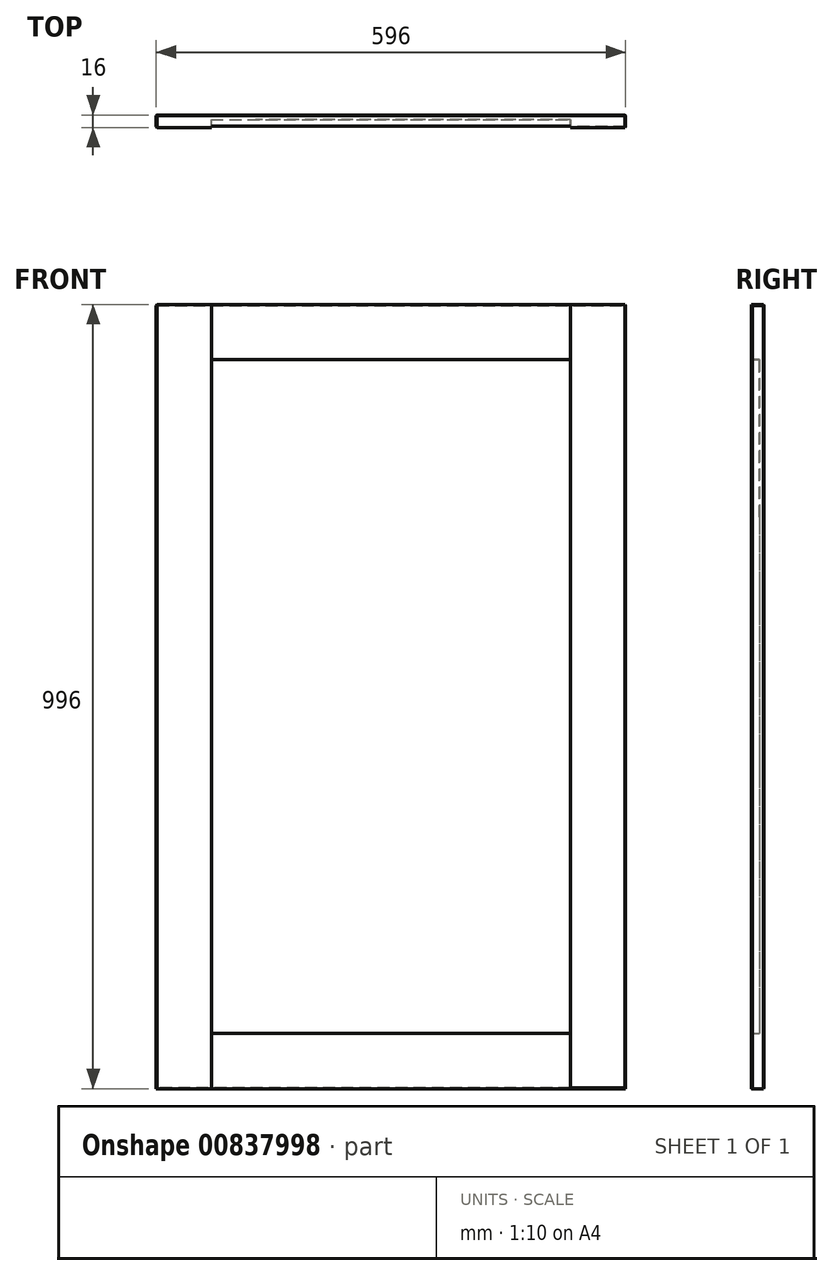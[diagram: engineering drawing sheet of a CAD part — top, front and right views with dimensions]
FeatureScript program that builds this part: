
annotation { "Feature Type Name" : "Feature", "Feature Type Description" : "" }
export const myFeature = defineFeature(function(context is Context, id is Id, definition is map)
    precondition{}
    {
        {
            var Q0;
            Q0=qCreatedBy(makeId("Front.planeOp"),FACE);
            var sketch = newSketch(context, id + "F0", { "sketchPlane" : qUnion([Q0])});
            skLineSegment(sketch, "E0.bottom", {"start": v(0, 0) * mm, "end": v(35.9, 0) * mm});
            skLineSegment(sketch, "E0.top", {"start": v(0, 30.12) * mm, "end": v(35.9, 30.12) * mm});
            skLineSegment(sketch, "E0.left", {"start": v(0, 0) * mm, "end": v(0, 30.12) * mm});
            skLineSegment(sketch, "E0.right", {"start": v(35.9, 0) * mm, "end": v(35.9, 30.12) * mm});
            skSolve(sketch);
        }
        {
            var Q0;
            Q0=makeQuery(id+"F0.imprint","IMPRINT",FACE,{"disambiguationData":[TD([[makeQuery(id+"F0.imprint","IMPRINT",EDGE,{"derivedFrom":sQuery(id+"F0.wireOp",EDGE,"E0.bottom")}),1.0]])]});
            extrude(context, id + "F1", {"entities" : qUnion([Q0]), "depth" : 16 * mm, "offsetDistance" : 25.4 * mm});
        }
        {
            var Q0;
            Q0=makeQuery(id+"F1.opExtrude","SWEPT_FACE",FACE,{"disambiguationData":[OSD([sQuery(id+"F0.wireOp",EDGE,"E0.left")])]});
            extrude(context, id + "F2", {"entities" : qUnion([Q0]), "operationType" : NewBodyOperationType.ADD, "oppositeDirection" : true, "depth" : 196 * mm, "offsetDistance" : 25 * mm});
        }
        {
            var Q0;
            {var subQ0=sQuery(id+"F0.wireOp",EDGE,"E0.bottom");Q0=makeQuery(id+"F2.boolean.opBoolean","MERGE",FACE,{"derivedFrom":[makeQuery(id+"F1.opExtrude","SWEPT_FACE",FACE,{"disambiguationData":[OSD([subQ0])]}),makeQuery(id+"F2.opExtrude","SWEPT_FACE",FACE,{"disambiguationData":[OSD([subQ0,sQuery(id+"F0.wireOp",EDGE,"E0.left")])]})]});}
            extrude(context, id + "F3", {"entities" : qUnion([Q0]), "operationType" : NewBodyOperationType.ADD, "oppositeDirection" : true, "depth" : 796 * mm, "offsetDistance" : 25 * mm});
        }
        {
            var Q0;
            {var subQ0=sQuery(id+"F0.wireOp",EDGE,"E0.left");var subQ1=sQuery(id+"F0.wireOp",EDGE,"E0.bottom");Q0=makeQuery(id+"F3.boolean.opBoolean","MERGE",FACE,{"derivedFrom":[makeQuery(id+"F2.boolean.opBoolean","MERGE",FACE,{"derivedFrom":[makeQuery(id+"F1.opExtrude","CAP_FACE",FACE,{"disambiguationData":[OSD([subQ1,sQuery(id+"F0.wireOp",EDGE,"E0.top"),subQ0,sQuery(id+"F0.wireOp",EDGE,"E0.right")])],"isStart":false}),makeQuery(id+"F2.opExtrude","SWEPT_FACE",FACE,{"disambiguationData":[OSD([subQ0]),TDD([makeQuery(id+"F1.opExtrude","CAP_EDGE",EDGE,{"disambiguationData":[OSD([subQ0])],"isStart":false})])]})]}),makeQuery(id+"F3.opExtrude","SWEPT_FACE",FACE,{"disambiguationData":[OSD([subQ1,subQ0]),TDD([makeQuery(id+"F2.boolean.opBoolean","MERGE",EDGE,{"derivedFrom":[makeQuery(id+"F1.opExtrude","CAP_EDGE",EDGE,{"disambiguationData":[OSD([subQ1])],"isStart":false}),makeQuery(id+"F2.opExtrude","SWEPT_EDGE",EDGE,{"disambiguationData":[OSD([subQ1,subQ0]),TDD([makeQuery(id+"F1.opExtrude","CAP_VERTEX",VERTEX,{"disambiguationData":[OSD([subQ1,subQ0])],"isStart":false})])]})]})])]})]});}
            var sketch = newSketch(context, id + "F4", { "sketchPlane" : qUnion([Q0])});
            skLineSegment(sketch, "E1.bottom", {"start": v(0, 796) * mm, "end": v(42.19, 796) * mm});
            skLineSegment(sketch, "E1.top", {"start": v(0, 751.57) * mm, "end": v(42.19, 751.57) * mm});
            skLineSegment(sketch, "E1.left", {"start": v(0, 796) * mm, "end": v(0, 751.57) * mm});
            skLineSegment(sketch, "E1.right", {"start": v(42.19, 796) * mm, "end": v(42.19, 751.57) * mm});
            skLineSegment(sketch, "E2.bottom", {"start": v(196, 796) * mm, "end": v(153.6, 796) * mm});
            skLineSegment(sketch, "E2.top", {"start": v(196, 746.75) * mm, "end": v(153.6, 746.75) * mm});
            skLineSegment(sketch, "E2.left", {"start": v(196, 796) * mm, "end": v(196, 746.75) * mm});
            skLineSegment(sketch, "E2.right", {"start": v(153.6, 796) * mm, "end": v(153.6, 746.75) * mm});
            skSolve(sketch);
        }
        {
            var Q0;
            Q0=makeQuery(id+"F4.imprint","IMPRINT",FACE,{"disambiguationData":[TD([[makeQuery(id+"F4.imprint","IMPRINT",EDGE,{"derivedFrom":sQuery(id+"F4.wireOp",EDGE,"E1.bottom")}),-1.0]])]});
            var Q1;
            Q1=makeQuery(id+"F4.imprint","IMPRINT",FACE,{"disambiguationData":[TD([[makeQuery(id+"F4.imprint","IMPRINT",EDGE,{"derivedFrom":sQuery(id+"F4.wireOp",EDGE,"E2.bottom")}),-1.0]])]});
            extrude(context, id + "F5", {"entities" : qUnion([Q0, Q1]), "operationType" : NewBodyOperationType.ADD, "depth" : 25 * mm, "offsetDistance" : 25 * mm});
        }
        {
            var Q0;
            {var subQ0=sQuery(id+"F0.wireOp",EDGE,"E0.left");var subQ1=sQuery(id+"F0.wireOp",EDGE,"E0.bottom");Q0=makeQuery(id+"F3.boolean.opBoolean","MERGE",FACE,{"derivedFrom":[makeQuery(id+"F2.boolean.opBoolean","MERGE",FACE,{"derivedFrom":[makeQuery(id+"F1.opExtrude","CAP_FACE",FACE,{"disambiguationData":[OSD([subQ1,sQuery(id+"F0.wireOp",EDGE,"E0.top"),subQ0,sQuery(id+"F0.wireOp",EDGE,"E0.right")])],"isStart":false}),makeQuery(id+"F2.opExtrude","SWEPT_FACE",FACE,{"disambiguationData":[OSD([subQ0]),TDD([makeQuery(id+"F1.opExtrude","CAP_EDGE",EDGE,{"disambiguationData":[OSD([subQ0])],"isStart":false})])]})]}),makeQuery(id+"F3.opExtrude","SWEPT_FACE",FACE,{"disambiguationData":[OSD([subQ1,subQ0]),TDD([makeQuery(id+"F2.boolean.opBoolean","MERGE",EDGE,{"derivedFrom":[makeQuery(id+"F1.opExtrude","CAP_EDGE",EDGE,{"disambiguationData":[OSD([subQ1])],"isStart":false}),makeQuery(id+"F2.opExtrude","SWEPT_EDGE",EDGE,{"disambiguationData":[OSD([subQ1,subQ0]),TDD([makeQuery(id+"F1.opExtrude","CAP_VERTEX",VERTEX,{"disambiguationData":[OSD([subQ1,subQ0])],"isStart":false})])]})]})])]})]});}
            var sketch = newSketch(context, id + "F6", { "sketchPlane" : qUnion([Q0])});
            skLineSegment(sketch, "E3.bottom", {"start": v(196, 0) * mm, "end": v(163.38, 0) * mm});
            skLineSegment(sketch, "E3.top", {"start": v(196, 46.55) * mm, "end": v(163.38, 46.55) * mm});
            skLineSegment(sketch, "E3.left", {"start": v(196, 0) * mm, "end": v(196, 46.55) * mm});
            skLineSegment(sketch, "E3.right", {"start": v(163.38, 0) * mm, "end": v(163.38, 46.55) * mm});
            skLineSegment(sketch, "E4.bottom", {"start": v(0, 0) * mm, "end": v(50.28, 0) * mm});
            skLineSegment(sketch, "E4.top", {"start": v(0, 44.4) * mm, "end": v(50.28, 44.4) * mm});
            skLineSegment(sketch, "E4.left", {"start": v(0, 0) * mm, "end": v(0, 44.4) * mm});
            skLineSegment(sketch, "E4.right", {"start": v(50.28, 0) * mm, "end": v(50.28, 44.4) * mm});
            skSolve(sketch);
        }
        {
            var Q0;
            Q0=makeQuery(id+"F6.imprint","IMPRINT",FACE,{"disambiguationData":[TD([[makeQuery(id+"F6.imprint","IMPRINT",EDGE,{"derivedFrom":sQuery(id+"F6.wireOp",EDGE,"E3.bottom")}),1.0]])]});
            var Q1;
            Q1=makeQuery(id+"F6.imprint","IMPRINT",FACE,{"disambiguationData":[TD([[makeQuery(id+"F6.imprint","IMPRINT",EDGE,{"derivedFrom":sQuery(id+"F6.wireOp",EDGE,"E4.bottom")}),1.0]])]});
            extrude(context, id + "F7", {"entities" : qUnion([Q0, Q1]), "operationType" : NewBodyOperationType.ADD, "depth" : 25 * mm, "offsetDistance" : 25 * mm});
        }
        {
            var Q0;
            Q0=makeQuery(id+"F7.opExtrude","SWEPT_FACE",FACE,{"disambiguationData":[OSD([sQuery(id+"F6.wireOp",EDGE,"E4.right")])]});
            extrude(context, id + "F8", {"entities" : qUnion([Q0]), "operationType" : NewBodyOperationType.ADD, "depth" : 19.72 * mm, "offsetDistance" : 25 * mm});
        }
        {
            var Q0;
            {var subQ0=sQuery(id+"F6.wireOp",EDGE,"E4.top");Q0=makeQuery(id+"F8.boolean.opBoolean","MERGE",FACE,{"derivedFrom":[makeQuery(id+"F7.opExtrude","SWEPT_FACE",FACE,{"disambiguationData":[OSD([subQ0])]}),makeQuery(id+"F8.opExtrude","SWEPT_FACE",FACE,{"disambiguationData":[OSD([subQ0,sQuery(id+"F6.wireOp",EDGE,"E4.right")])]})]});}
            extrude(context, id + "F9", {"entities" : qUnion([Q0]), "operationType" : NewBodyOperationType.ADD, "depth" : 25.6 * mm, "offsetDistance" : 25 * mm});
        }
        {
            var Q0;
            Q0=makeQuery(id+"F7.opExtrude","SWEPT_FACE",FACE,{"disambiguationData":[OSD([sQuery(id+"F6.wireOp",EDGE,"E3.right")])]});
            extrude(context, id + "F10", {"entities" : qUnion([Q0]), "operationType" : NewBodyOperationType.ADD, "depth" : 37.38 * mm, "offsetDistance" : 25 * mm});
        }
        {
            var Q0;
            {var subQ0=sQuery(id+"F6.wireOp",EDGE,"E3.top");Q0=makeQuery(id+"F10.boolean.opBoolean","MERGE",FACE,{"derivedFrom":[makeQuery(id+"F7.opExtrude","SWEPT_FACE",FACE,{"disambiguationData":[OSD([subQ0])]}),makeQuery(id+"F10.opExtrude","SWEPT_FACE",FACE,{"disambiguationData":[OSD([subQ0,sQuery(id+"F6.wireOp",EDGE,"E3.right")])]})]});}
            extrude(context, id + "F11", {"entities" : qUnion([Q0]), "operationType" : NewBodyOperationType.ADD, "depth" : 23.45 * mm, "offsetDistance" : 25 * mm});
        }
        {
            var Q0;
            Q0=makeQuery(id+"F5.opExtrude","SWEPT_FACE",FACE,{"disambiguationData":[OSD([sQuery(id+"F4.wireOp",EDGE,"E1.right")])]});
            extrude(context, id + "F12", {"entities" : qUnion([Q0]), "operationType" : NewBodyOperationType.ADD, "depth" : 27.8 * mm, "offsetDistance" : 25 * mm});
        }
        {
            var Q0;
            {var subQ0=sQuery(id+"F4.wireOp",EDGE,"E1.top");Q0=makeQuery(id+"F12.boolean.opBoolean","MERGE",FACE,{"derivedFrom":[makeQuery(id+"F5.opExtrude","SWEPT_FACE",FACE,{"disambiguationData":[OSD([subQ0])]}),makeQuery(id+"F12.opExtrude","SWEPT_FACE",FACE,{"disambiguationData":[OSD([subQ0,sQuery(id+"F4.wireOp",EDGE,"E1.right")])]})]});}
            extrude(context, id + "F13", {"entities" : qUnion([Q0]), "operationType" : NewBodyOperationType.ADD, "depth" : 25.57 * mm, "offsetDistance" : 25 * mm});
        }
        {
            var Q0;
            Q0=makeQuery(id+"F5.opExtrude","SWEPT_FACE",FACE,{"disambiguationData":[OSD([sQuery(id+"F4.wireOp",EDGE,"E2.top")])]});
            extrude(context, id + "F14", {"entities" : qUnion([Q0]), "operationType" : NewBodyOperationType.ADD, "depth" : 20.75 * mm, "offsetDistance" : 25 * mm});
        }
        {
            var Q0;
            {var subQ0=sQuery(id+"F4.wireOp",EDGE,"E2.right");Q0=makeQuery(id+"F14.boolean.opBoolean","MERGE",FACE,{"derivedFrom":[makeQuery(id+"F5.opExtrude","SWEPT_FACE",FACE,{"disambiguationData":[OSD([subQ0])]}),makeQuery(id+"F14.opExtrude","SWEPT_FACE",FACE,{"disambiguationData":[OSD([sQuery(id+"F4.wireOp",EDGE,"E2.top"),subQ0])]})]});}
            extrude(context, id + "F15", {"entities" : qUnion([Q0]), "operationType" : NewBodyOperationType.ADD, "depth" : 27.6 * mm, "offsetDistance" : 25 * mm});
        }
        {
            var Q0;
            {var subQ0=sQuery(id+"F0.wireOp",EDGE,"E0.left");var subQ1=sQuery(id+"F0.wireOp",EDGE,"E0.bottom");Q0=makeQuery(id+"F3.boolean.opBoolean","MERGE",FACE,{"derivedFrom":[makeQuery(id+"F2.boolean.opBoolean","MERGE",FACE,{"derivedFrom":[makeQuery(id+"F1.opExtrude","CAP_FACE",FACE,{"disambiguationData":[OSD([subQ1,sQuery(id+"F0.wireOp",EDGE,"E0.top"),subQ0,sQuery(id+"F0.wireOp",EDGE,"E0.right")])],"isStart":false}),makeQuery(id+"F2.opExtrude","SWEPT_FACE",FACE,{"disambiguationData":[OSD([subQ0]),TDD([makeQuery(id+"F1.opExtrude","CAP_EDGE",EDGE,{"disambiguationData":[OSD([subQ0])],"isStart":false})])]})]}),makeQuery(id+"F3.opExtrude","SWEPT_FACE",FACE,{"disambiguationData":[OSD([subQ1,subQ0]),TDD([makeQuery(id+"F2.boolean.opBoolean","MERGE",EDGE,{"derivedFrom":[makeQuery(id+"F1.opExtrude","CAP_EDGE",EDGE,{"disambiguationData":[OSD([subQ1])],"isStart":false}),makeQuery(id+"F2.opExtrude","SWEPT_EDGE",EDGE,{"disambiguationData":[OSD([subQ1,subQ0]),TDD([makeQuery(id+"F1.opExtrude","CAP_VERTEX",VERTEX,{"disambiguationData":[OSD([subQ1,subQ0])],"isStart":false})])]})]})])]})]});}
            var sketch = newSketch(context, id + "F16", { "sketchPlane" : qUnion([Q0])});
            skLineSegment(sketch, "E5.bottom", {"start": v(70, 726) * mm, "end": v(126, 726) * mm});
            skLineSegment(sketch, "E5.top", {"start": v(70, 70) * mm, "end": v(126, 70) * mm});
            skLineSegment(sketch, "E5.left", {"start": v(70, 726) * mm, "end": v(70, 70) * mm});
            skLineSegment(sketch, "E5.right", {"start": v(126, 726) * mm, "end": v(126, 70) * mm});
            skSolve(sketch);
        }
        {
            var Q0;
            Q0=makeQuery(id+"F16.imprint","IMPRINT",FACE,{"disambiguationData":[TD([[makeQuery(id+"F16.imprint","IMPRINT",EDGE,{"derivedFrom":sQuery(id+"F16.wireOp",EDGE,"E5.top")}),1.0]])]});
            extrude(context, id + "F17", {"entities" : qUnion([Q0]), "operationType" : NewBodyOperationType.REMOVE, "oppositeDirection" : true, "depth" : 10 * mm, "offsetDistance" : 25 * mm});
        }
        {
            var Q0;
            {var subQ2=sQuery(id+"F0.wireOp",EDGE,"E0.left");var subQ3=sQuery(id+"F0.wireOp",EDGE,"E0.bottom");var subQ4=makeQuery(id+"F1.opExtrude","CAP_FACE",FACE,{"disambiguationData":[OSD([subQ3,sQuery(id+"F0.wireOp",EDGE,"E0.top"),subQ2,sQuery(id+"F0.wireOp",EDGE,"E0.right")])],"isStart":false});var subQ7=makeQuery(id+"F3.opExtrude","SWEPT_FACE",FACE,{"disambiguationData":[OSD([subQ3,subQ2]),TDD([makeQuery(id+"F2.boolean.opBoolean","MERGE",EDGE,{"derivedFrom":[makeQuery(id+"F1.opExtrude","CAP_EDGE",EDGE,{"disambiguationData":[OSD([subQ3])],"isStart":false}),makeQuery(id+"F2.opExtrude","SWEPT_EDGE",EDGE,{"disambiguationData":[OSD([subQ3,subQ2]),TDD([makeQuery(id+"F1.opExtrude","CAP_VERTEX",VERTEX,{"disambiguationData":[OSD([subQ3,subQ2])],"isStart":false})])]})]})])]});var subQ8=makeQuery(id+"F2.opExtrude","SWEPT_FACE",FACE,{"disambiguationData":[OSD([subQ2]),TDD([makeQuery(id+"F1.opExtrude","CAP_EDGE",EDGE,{"disambiguationData":[OSD([subQ2])],"isStart":false})])]});Q0=makeQuery(id+"F17.boolean.opBoolean","SPLIT",FACE,{"disambiguationData":[TD([makeQuery(id+"F1.opExtrude","SWEPT_FACE",FACE,{"disambiguationData":[OSD([subQ3])]})])],"derivedFrom":makeQuery(id+"F3.boolean.opBoolean","MERGE",FACE,{"derivedFrom":[makeQuery(id+"F2.boolean.opBoolean","MERGE",FACE,{"derivedFrom":[subQ4,subQ8]}),subQ7]})});}
            var Q1;
            {var subQ2=sQuery(id+"F4.wireOp",EDGE,"E1.bottom");var subQ3=sQuery(id+"F0.wireOp",EDGE,"E0.left");var subQ4=sQuery(id+"F0.wireOp",EDGE,"E0.bottom");var subQ6=makeQuery(id+"F1.opExtrude","CAP_FACE",FACE,{"disambiguationData":[OSD([subQ4,sQuery(id+"F0.wireOp",EDGE,"E0.top"),subQ3,sQuery(id+"F0.wireOp",EDGE,"E0.right")])],"isStart":false});var subQ7=makeQuery(id+"F2.opExtrude","SWEPT_FACE",FACE,{"disambiguationData":[OSD([subQ3]),TDD([makeQuery(id+"F1.opExtrude","CAP_EDGE",EDGE,{"disambiguationData":[OSD([subQ3])],"isStart":false})])]});var subQ8=makeQuery(id+"F3.opExtrude","SWEPT_FACE",FACE,{"disambiguationData":[OSD([subQ4,subQ3]),TDD([makeQuery(id+"F2.boolean.opBoolean","MERGE",EDGE,{"derivedFrom":[makeQuery(id+"F1.opExtrude","CAP_EDGE",EDGE,{"disambiguationData":[OSD([subQ4])],"isStart":false}),makeQuery(id+"F2.opExtrude","SWEPT_EDGE",EDGE,{"disambiguationData":[OSD([subQ4,subQ3]),TDD([makeQuery(id+"F1.opExtrude","CAP_VERTEX",VERTEX,{"disambiguationData":[OSD([subQ4,subQ3])],"isStart":false})])]})]})])]});Q1=makeQuery(id+"F17.boolean.opBoolean","SPLIT",FACE,{"disambiguationData":[TD([makeQuery(id+"F5.opExtrude","SWEPT_FACE",FACE,{"disambiguationData":[OSD([subQ2])]})])],"derivedFrom":makeQuery(id+"F3.boolean.opBoolean","MERGE",FACE,{"derivedFrom":[makeQuery(id+"F2.boolean.opBoolean","MERGE",FACE,{"derivedFrom":[subQ6,subQ7]}),subQ8]})});}
            extrude(context, id + "F18", {"entities" : qUnion([Q0, Q1]), "operationType" : NewBodyOperationType.REMOVE, "oppositeDirection" : true, "depth" : 2 * mm, "offsetDistance" : 25 * mm});
        }
        {
            var Q0;
            {var subQ0=sQuery(id+"F4.wireOp",EDGE,"E1.right");var subQ1=sQuery(id+"F4.wireOp",EDGE,"E1.top");Q0=makeQuery(id+"F13.boolean.opBoolean","MERGE",FACE,{"derivedFrom":[makeQuery(id+"F12.boolean.opBoolean","MERGE",FACE,{"derivedFrom":[makeQuery(id+"F5.opExtrude","CAP_FACE",FACE,{"disambiguationData":[OSD([sQuery(id+"F4.wireOp",EDGE,"E1.bottom"),subQ1,sQuery(id+"F4.wireOp",EDGE,"E1.left"),subQ0])],"isStart":false}),makeQuery(id+"F12.opExtrude","SWEPT_FACE",FACE,{"disambiguationData":[OSD([subQ0]),TDD([makeQuery(id+"F5.opExtrude","CAP_EDGE",EDGE,{"disambiguationData":[OSD([subQ0])],"isStart":false})])]})]}),makeQuery(id+"F13.opExtrude","SWEPT_FACE",FACE,{"disambiguationData":[OSD([subQ1,subQ0]),TDD([makeQuery(id+"F12.boolean.opBoolean","MERGE",EDGE,{"derivedFrom":[makeQuery(id+"F5.opExtrude","CAP_EDGE",EDGE,{"disambiguationData":[OSD([subQ1])],"isStart":false}),makeQuery(id+"F12.opExtrude","SWEPT_EDGE",EDGE,{"disambiguationData":[OSD([subQ1,subQ0]),TDD([makeQuery(id+"F5.opExtrude","CAP_VERTEX",VERTEX,{"disambiguationData":[OSD([subQ1,subQ0])],"isStart":false})])]})]})])]})]});}
            var Q1;
            {var subQ0=sQuery(id+"F4.wireOp",EDGE,"E2.right");var subQ1=sQuery(id+"F4.wireOp",EDGE,"E2.top");Q1=makeQuery(id+"F15.boolean.opBoolean","MERGE",FACE,{"derivedFrom":[makeQuery(id+"F14.boolean.opBoolean","MERGE",FACE,{"derivedFrom":[makeQuery(id+"F5.opExtrude","CAP_FACE",FACE,{"disambiguationData":[OSD([sQuery(id+"F4.wireOp",EDGE,"E2.bottom"),subQ1,sQuery(id+"F4.wireOp",EDGE,"E2.left"),subQ0])],"isStart":false}),makeQuery(id+"F14.opExtrude","SWEPT_FACE",FACE,{"disambiguationData":[OSD([subQ1]),TDD([makeQuery(id+"F5.opExtrude","CAP_EDGE",EDGE,{"disambiguationData":[OSD([subQ1])],"isStart":false})])]})]}),makeQuery(id+"F15.opExtrude","SWEPT_FACE",FACE,{"disambiguationData":[OSD([subQ1,subQ0]),TDD([makeQuery(id+"F14.boolean.opBoolean","MERGE",EDGE,{"derivedFrom":[makeQuery(id+"F5.opExtrude","CAP_EDGE",EDGE,{"disambiguationData":[OSD([subQ0])],"isStart":false}),makeQuery(id+"F14.opExtrude","SWEPT_EDGE",EDGE,{"disambiguationData":[OSD([subQ1,subQ0]),TDD([makeQuery(id+"F5.opExtrude","CAP_VERTEX",VERTEX,{"disambiguationData":[OSD([subQ1,subQ0])],"isStart":false})])]})]})])]})]});}
            var Q2;
            {var subQ0=sQuery(id+"F6.wireOp",EDGE,"E4.right");var subQ1=sQuery(id+"F6.wireOp",EDGE,"E4.top");Q2=makeQuery(id+"F9.boolean.opBoolean","MERGE",FACE,{"derivedFrom":[makeQuery(id+"F8.boolean.opBoolean","MERGE",FACE,{"derivedFrom":[makeQuery(id+"F7.opExtrude","CAP_FACE",FACE,{"disambiguationData":[OSD([sQuery(id+"F6.wireOp",EDGE,"E4.bottom"),subQ1,sQuery(id+"F6.wireOp",EDGE,"E4.left"),subQ0])],"isStart":false}),makeQuery(id+"F8.opExtrude","SWEPT_FACE",FACE,{"disambiguationData":[OSD([subQ0]),TDD([makeQuery(id+"F7.opExtrude","CAP_EDGE",EDGE,{"disambiguationData":[OSD([subQ0])],"isStart":false})])]})]}),makeQuery(id+"F9.opExtrude","SWEPT_FACE",FACE,{"disambiguationData":[OSD([subQ1,subQ0]),TDD([makeQuery(id+"F8.boolean.opBoolean","MERGE",EDGE,{"derivedFrom":[makeQuery(id+"F7.opExtrude","CAP_EDGE",EDGE,{"disambiguationData":[OSD([subQ1])],"isStart":false}),makeQuery(id+"F8.opExtrude","SWEPT_EDGE",EDGE,{"disambiguationData":[OSD([subQ1,subQ0]),TDD([makeQuery(id+"F7.opExtrude","CAP_VERTEX",VERTEX,{"disambiguationData":[OSD([subQ1,subQ0])],"isStart":false})])]})]})])]})]});}
            var Q3;
            {var subQ0=sQuery(id+"F6.wireOp",EDGE,"E3.right");var subQ1=sQuery(id+"F6.wireOp",EDGE,"E3.top");Q3=makeQuery(id+"F11.boolean.opBoolean","MERGE",FACE,{"derivedFrom":[makeQuery(id+"F10.boolean.opBoolean","MERGE",FACE,{"derivedFrom":[makeQuery(id+"F7.opExtrude","CAP_FACE",FACE,{"disambiguationData":[OSD([sQuery(id+"F6.wireOp",EDGE,"E3.bottom"),subQ1,sQuery(id+"F6.wireOp",EDGE,"E3.left"),subQ0])],"isStart":false}),makeQuery(id+"F10.opExtrude","SWEPT_FACE",FACE,{"disambiguationData":[OSD([subQ0]),TDD([makeQuery(id+"F7.opExtrude","CAP_EDGE",EDGE,{"disambiguationData":[OSD([subQ0])],"isStart":false})])]})]}),makeQuery(id+"F11.opExtrude","SWEPT_FACE",FACE,{"disambiguationData":[OSD([subQ1,subQ0]),TDD([makeQuery(id+"F10.boolean.opBoolean","MERGE",EDGE,{"derivedFrom":[makeQuery(id+"F7.opExtrude","CAP_EDGE",EDGE,{"disambiguationData":[OSD([subQ1])],"isStart":false}),makeQuery(id+"F10.opExtrude","SWEPT_EDGE",EDGE,{"disambiguationData":[OSD([subQ1,subQ0]),TDD([makeQuery(id+"F7.opExtrude","CAP_VERTEX",VERTEX,{"disambiguationData":[OSD([subQ1,subQ0])],"isStart":false})])]})]})])]})]});}
            extrude(context, id + "F19", {"entities" : qUnion([Q0, Q1, Q2, Q3]), "operationType" : NewBodyOperationType.REMOVE, "oppositeDirection" : true, "depth" : 25 * mm, "offsetDistance" : 25 * mm});
        }
        {
            var Q0;
            {var subQ0=sQuery(id+"F4.wireOp",EDGE,"E2.left");var subQ1=sQuery(id+"F0.wireOp",EDGE,"E0.left");var subQ2=sQuery(id+"F0.wireOp",EDGE,"E0.bottom");var subQ3=sQuery(id+"F6.wireOp",EDGE,"E3.left");Q0=makeQuery(id+"F14.boolean.opBoolean","MERGE",FACE,{"derivedFrom":[makeQuery(id+"F11.boolean.opBoolean","MERGE",FACE,{"derivedFrom":[makeQuery(id+"F7.boolean.opBoolean","MERGE",FACE,{"derivedFrom":[makeQuery(id+"F5.boolean.opBoolean","MERGE",FACE,{"derivedFrom":[makeQuery(id+"F3.boolean.opBoolean","MERGE",FACE,{"derivedFrom":[makeQuery(id+"F2.opExtrude","CAP_FACE",FACE,{"disambiguationData":[OSD([subQ1])],"isStart":false}),makeQuery(id+"F3.opExtrude","SWEPT_FACE",FACE,{"disambiguationData":[OSD([subQ2,subQ1]),TDD([makeQuery(id+"F2.opExtrude","CAP_EDGE",EDGE,{"disambiguationData":[OSD([subQ2,subQ1])],"isStart":false})])]})]}),makeQuery(id+"F5.opExtrude","SWEPT_FACE",FACE,{"disambiguationData":[OSD([subQ0])]})]}),makeQuery(id+"F7.opExtrude","SWEPT_FACE",FACE,{"disambiguationData":[OSD([subQ3])]})]}),makeQuery(id+"F11.opExtrude","SWEPT_FACE",FACE,{"disambiguationData":[OSD([subQ2,subQ1,sQuery(id+"F6.wireOp",EDGE,"E3.top"),subQ3])]})]}),makeQuery(id+"F14.opExtrude","SWEPT_FACE",FACE,{"disambiguationData":[OSD([subQ2,subQ1,sQuery(id+"F4.wireOp",EDGE,"E2.top"),subQ0])]})]});}
            extrude(context, id + "F20", {"entities" : qUnion([Q0]), "operationType" : NewBodyOperationType.ADD, "depth" : 400 * mm, "offsetDistance" : 25 * mm});
        }
        {
            var Q0;
            {var subQ0=sQuery(id+"F6.wireOp",EDGE,"E3.right");var subQ1=sQuery(id+"F6.wireOp",EDGE,"E3.top");Q0=makeQuery(id+"F18.boolean.opBoolean","MERGE",FACE,{"derivedFrom":[makeQuery(id+"F11.boolean.opBoolean","MERGE",FACE,{"derivedFrom":[makeQuery(id+"F10.opExtrude","CAP_FACE",FACE,{"disambiguationData":[OSD([subQ0])],"isStart":false}),makeQuery(id+"F11.opExtrude","SWEPT_FACE",FACE,{"disambiguationData":[OSD([subQ1,subQ0]),TDD([makeQuery(id+"F10.opExtrude","CAP_EDGE",EDGE,{"disambiguationData":[OSD([subQ1,subQ0])],"isStart":false})])]})]}),makeQuery(id+"F17.boolean.opBoolean","COPY",FACE,{"derivedFrom":makeQuery(id+"F17.opExtrude","SWEPT_FACE",FACE,{"disambiguationData":[OSD([sQuery(id+"F16.wireOp",EDGE,"E5.right")])]})}),makeQuery(id+"F18.opExtrude","SWEPT_FACE",FACE,{"disambiguationData":[OSD([subQ1,subQ0])]})]});}
            var Q1;
            {var subQ0=sQuery(id+"F4.wireOp",EDGE,"E2.right");var subQ1=sQuery(id+"F4.wireOp",EDGE,"E2.top");Q1=makeQuery(id+"F18.boolean.opBoolean","MERGE",FACE,{"derivedFrom":[makeQuery(id+"F15.opExtrude","CAP_FACE",FACE,{"disambiguationData":[OSD([subQ1,subQ0])],"isStart":false}),makeQuery(id+"F18.opExtrude","SWEPT_FACE",FACE,{"disambiguationData":[OSD([subQ1,subQ0])]})]});}
            extrude(context, id + "F21", {"entities" : qUnion([Q0, Q1]), "operationType" : NewBodyOperationType.REMOVE, "oppositeDirection" : true, "depth" : 400 * mm, "offsetDistance" : 25 * mm});
        }
        {
            var Q0;
            {var subQ0=sQuery(id+"F4.wireOp",EDGE,"E2.bottom");var subQ1=sQuery(id+"F0.wireOp",EDGE,"E0.left");var subQ2=sQuery(id+"F0.wireOp",EDGE,"E0.bottom");var subQ3=sQuery(id+"F4.wireOp",EDGE,"E1.bottom");Q0=makeQuery(id+"F20.boolean.opBoolean","MERGE",FACE,{"derivedFrom":[makeQuery(id+"F15.boolean.opBoolean","MERGE",FACE,{"derivedFrom":[makeQuery(id+"F12.boolean.opBoolean","MERGE",FACE,{"derivedFrom":[makeQuery(id+"F5.boolean.opBoolean","MERGE",FACE,{"derivedFrom":[makeQuery(id+"F3.opExtrude","CAP_FACE",FACE,{"disambiguationData":[OSD([subQ2,subQ1])],"isStart":false}),makeQuery(id+"F5.opExtrude","SWEPT_FACE",FACE,{"disambiguationData":[OSD([subQ3])]}),makeQuery(id+"F5.opExtrude","SWEPT_FACE",FACE,{"disambiguationData":[OSD([subQ0])]})]}),makeQuery(id+"F12.opExtrude","SWEPT_FACE",FACE,{"disambiguationData":[OSD([subQ2,subQ1,subQ3,sQuery(id+"F4.wireOp",EDGE,"E1.right")])]})]}),makeQuery(id+"F15.opExtrude","SWEPT_FACE",FACE,{"disambiguationData":[OSD([subQ2,subQ1,subQ0,sQuery(id+"F4.wireOp",EDGE,"E2.right")])]})]}),makeQuery(id+"F20.opExtrude","SWEPT_FACE",FACE,{"disambiguationData":[OSD([subQ2,subQ1,subQ0,sQuery(id+"F4.wireOp",EDGE,"E2.left")])]})]});}
            extrude(context, id + "F22", {"entities" : qUnion([Q0]), "operationType" : NewBodyOperationType.ADD, "depth" : 200 * mm, "offsetDistance" : 25 * mm});
        }
        {
            var Q0;
            Q0=makeQuery(id+"F17.boolean.opBoolean","COPY",FACE,{"derivedFrom":makeQuery(id+"F17.opExtrude","SWEPT_FACE",FACE,{"disambiguationData":[OSD([sQuery(id+"F16.wireOp",EDGE,"E5.bottom")])]})});
            var Q1;
            {var subQ0=sQuery(id+"F16.wireOp",EDGE,"E5.right");var subQ1=sQuery(id+"F16.wireOp",EDGE,"E5.bottom");var subQ2=sQuery(id+"F4.wireOp",EDGE,"E2.right");var subQ3=sQuery(id+"F4.wireOp",EDGE,"E2.top");var subQ4=makeQuery(id+"F17.boolean.opBoolean","COPY",EDGE,{"derivedFrom":makeQuery(id+"F17.opExtrude","SWEPT_EDGE",EDGE,{"disambiguationData":[OSD([subQ3,subQ2,subQ1,subQ0])]})});Q1=makeQuery(id+"F21.boolean.opBoolean","COPY",FACE,{"derivedFrom":makeQuery(id+"F21.opExtrude","SWEPT_FACE",FACE,{"disambiguationData":[OSD([subQ3,subQ2,subQ1,subQ0]),TDD([makeQuery(id+"F18.boolean.opBoolean","MERGE",EDGE,{"derivedFrom":[subQ4,makeQuery(id+"F18.opExtrude","SWEPT_EDGE",EDGE,{"disambiguationData":[OSD([subQ3,subQ2,subQ1,subQ0])]})]}),makeQuery(id+"F18.boolean.opBoolean","SPLIT",EDGE,{"derivedFrom":subQ4})])]})});}
            extrude(context, id + "F23", {"entities" : qUnion([Q0, Q1]), "operationType" : NewBodyOperationType.REMOVE, "oppositeDirection" : true, "depth" : 200 * mm, "offsetDistance" : 25 * mm});
        }
        {
            var Q0;
            {var subQ0=sQuery(id+"F4.wireOp",EDGE,"E1.right");var subQ1=sQuery(id+"F4.wireOp",EDGE,"E1.bottom");var subQ2=sQuery(id+"F0.wireOp",EDGE,"E0.left");var subQ3=sQuery(id+"F0.wireOp",EDGE,"E0.bottom");Q0=makeQuery(id+"F22.opExtrude","CAP_EDGE",EDGE,{"disambiguationData":[OSD([subQ3,subQ2,subQ1,subQ0]),TDD([makeQuery(id+"F19.boolean.opBoolean","COPY",EDGE,{"derivedFrom":makeQuery(id+"F19.opExtrude","CAP_EDGE",EDGE,{"disambiguationData":[OSD([subQ3,subQ2,subQ1,subQ0])],"isStart":false})})])],"isStart":false});}
            var Q1;
            {var subQ0=sQuery(id+"F4.wireOp",EDGE,"E1.left");var subQ1=sQuery(id+"F0.wireOp",EDGE,"E0.left");var subQ2=sQuery(id+"F0.wireOp",EDGE,"E0.bottom");Q1=makeQuery(id+"F22.boolean.opBoolean","MERGE",EDGE,{"derivedFrom":[makeQuery(id+"F19.boolean.opBoolean","MERGE",EDGE,{"derivedFrom":[makeQuery(id+"F3.boolean.opBoolean","MERGE",EDGE,{"derivedFrom":[makeQuery(id+"F1.opExtrude","CAP_EDGE",EDGE,{"disambiguationData":[OSD([subQ1])],"isStart":false}),makeQuery(id+"F3.opExtrude","SWEPT_EDGE",EDGE,{"disambiguationData":[OSD([subQ2,subQ1]),TDD([makeQuery(id+"F1.opExtrude","CAP_VERTEX",VERTEX,{"disambiguationData":[OSD([subQ2,subQ1])],"isStart":false})])]})]}),makeQuery(id+"F19.opExtrude","CAP_EDGE",EDGE,{"disambiguationData":[OSD([subQ2,subQ1,sQuery(id+"F6.wireOp",EDGE,"E4.top"),sQuery(id+"F6.wireOp",EDGE,"E4.left")])],"isStart":false}),makeQuery(id+"F19.opExtrude","CAP_EDGE",EDGE,{"disambiguationData":[OSD([subQ2,subQ1,sQuery(id+"F4.wireOp",EDGE,"E1.top"),subQ0])],"isStart":false})]}),makeQuery(id+"F22.opExtrude","SWEPT_EDGE",EDGE,{"disambiguationData":[OSD([sQuery(id+"F4.wireOp",EDGE,"E1.bottom"),subQ0])]})]});}
            var Q2;
            {var subQ0=sQuery(id+"F4.wireOp",EDGE,"E2.left");Q2=makeQuery(id+"F22.boolean.opBoolean","MERGE",EDGE,{"derivedFrom":[makeQuery(id+"F20.opExtrude","CAP_EDGE",EDGE,{"disambiguationData":[OSD([sQuery(id+"F0.wireOp",EDGE,"E0.bottom"),sQuery(id+"F0.wireOp",EDGE,"E0.left"),sQuery(id+"F4.wireOp",EDGE,"E2.top"),subQ0,sQuery(id+"F6.wireOp",EDGE,"E3.top"),sQuery(id+"F6.wireOp",EDGE,"E3.left")])],"isStart":false}),makeQuery(id+"F22.opExtrude","SWEPT_EDGE",EDGE,{"disambiguationData":[OSD([sQuery(id+"F4.wireOp",EDGE,"E2.bottom"),subQ0])]})]});}
            var Q3;
            Q3=makeQuery(id+"F22.opExtrude","CAP_EDGE",EDGE,{"disambiguationData":[OSD([sQuery(id+"F0.wireOp",EDGE,"E0.bottom"),sQuery(id+"F0.wireOp",EDGE,"E0.left"),sQuery(id+"F4.wireOp",EDGE,"E2.bottom"),sQuery(id+"F4.wireOp",EDGE,"E2.left"),sQuery(id+"F4.wireOp",EDGE,"E2.right")])],"isStart":false});
            var Q4;
            {var subQ0=sQuery(id+"F6.wireOp",EDGE,"E3.bottom");Q4=makeQuery(id+"F20.boolean.opBoolean","MERGE",EDGE,{"derivedFrom":[makeQuery(id+"F19.boolean.opBoolean","COPY",EDGE,{"derivedFrom":makeQuery(id+"F19.opExtrude","CAP_EDGE",EDGE,{"disambiguationData":[OSD([sQuery(id+"F0.wireOp",EDGE,"E0.bottom"),sQuery(id+"F0.wireOp",EDGE,"E0.left"),subQ0,sQuery(id+"F6.wireOp",EDGE,"E3.right")])],"isStart":false})}),makeQuery(id+"F20.opExtrude","SWEPT_EDGE",EDGE,{"disambiguationData":[OSD([subQ0,sQuery(id+"F6.wireOp",EDGE,"E3.left")])]})]});}
            var Q5;
            Q5=makeQuery(id+"F19.boolean.opBoolean","COPY",EDGE,{"derivedFrom":makeQuery(id+"F19.opExtrude","CAP_EDGE",EDGE,{"disambiguationData":[OSD([sQuery(id+"F0.wireOp",EDGE,"E0.bottom"),sQuery(id+"F0.wireOp",EDGE,"E0.left"),sQuery(id+"F6.wireOp",EDGE,"E4.bottom"),sQuery(id+"F6.wireOp",EDGE,"E4.right")])],"isStart":false})});
            var Q6;
            {var subQ0=sQuery(id+"F0.wireOp",EDGE,"E0.left");var subQ1=sQuery(id+"F0.wireOp",EDGE,"E0.bottom");Q6=makeQuery(id+"F22.boolean.opBoolean","MERGE",FACE,{"derivedFrom":[makeQuery(id+"F20.boolean.opBoolean","MERGE",FACE,{"derivedFrom":[makeQuery(id+"F3.boolean.opBoolean","MERGE",FACE,{"derivedFrom":[makeQuery(id+"F2.boolean.opBoolean","MERGE",FACE,{"derivedFrom":[makeQuery(id+"F1.opExtrude","CAP_FACE",FACE,{"disambiguationData":[OSD([subQ1,sQuery(id+"F0.wireOp",EDGE,"E0.top"),subQ0,sQuery(id+"F0.wireOp",EDGE,"E0.right")])],"isStart":true}),makeQuery(id+"F2.opExtrude","SWEPT_FACE",FACE,{"disambiguationData":[OSD([subQ0]),TDD([makeQuery(id+"F1.opExtrude","CAP_EDGE",EDGE,{"disambiguationData":[OSD([subQ0])],"isStart":true})])]})]}),makeQuery(id+"F3.opExtrude","SWEPT_FACE",FACE,{"disambiguationData":[OSD([subQ1,subQ0]),TDD([makeQuery(id+"F2.boolean.opBoolean","MERGE",EDGE,{"derivedFrom":[makeQuery(id+"F1.opExtrude","CAP_EDGE",EDGE,{"disambiguationData":[OSD([subQ1])],"isStart":true}),makeQuery(id+"F2.opExtrude","SWEPT_EDGE",EDGE,{"disambiguationData":[OSD([subQ1,subQ0]),TDD([makeQuery(id+"F1.opExtrude","CAP_VERTEX",VERTEX,{"disambiguationData":[OSD([subQ1,subQ0])],"isStart":true})])]})]})])]})]}),makeQuery(id+"F20.opExtrude","SWEPT_FACE",FACE,{"disambiguationData":[OSD([subQ1,subQ0])]})]}),makeQuery(id+"F22.opExtrude","SWEPT_FACE",FACE,{"disambiguationData":[OSD([subQ1,subQ0])]})]});}
            chamfer(context, id + "F24", {"entities" : qUnion([Q0, Q1, Q2, Q3, Q4, Q5, Q6]), "width" : 1 * mm, "tangentPropagation" : true});
        }
    });
